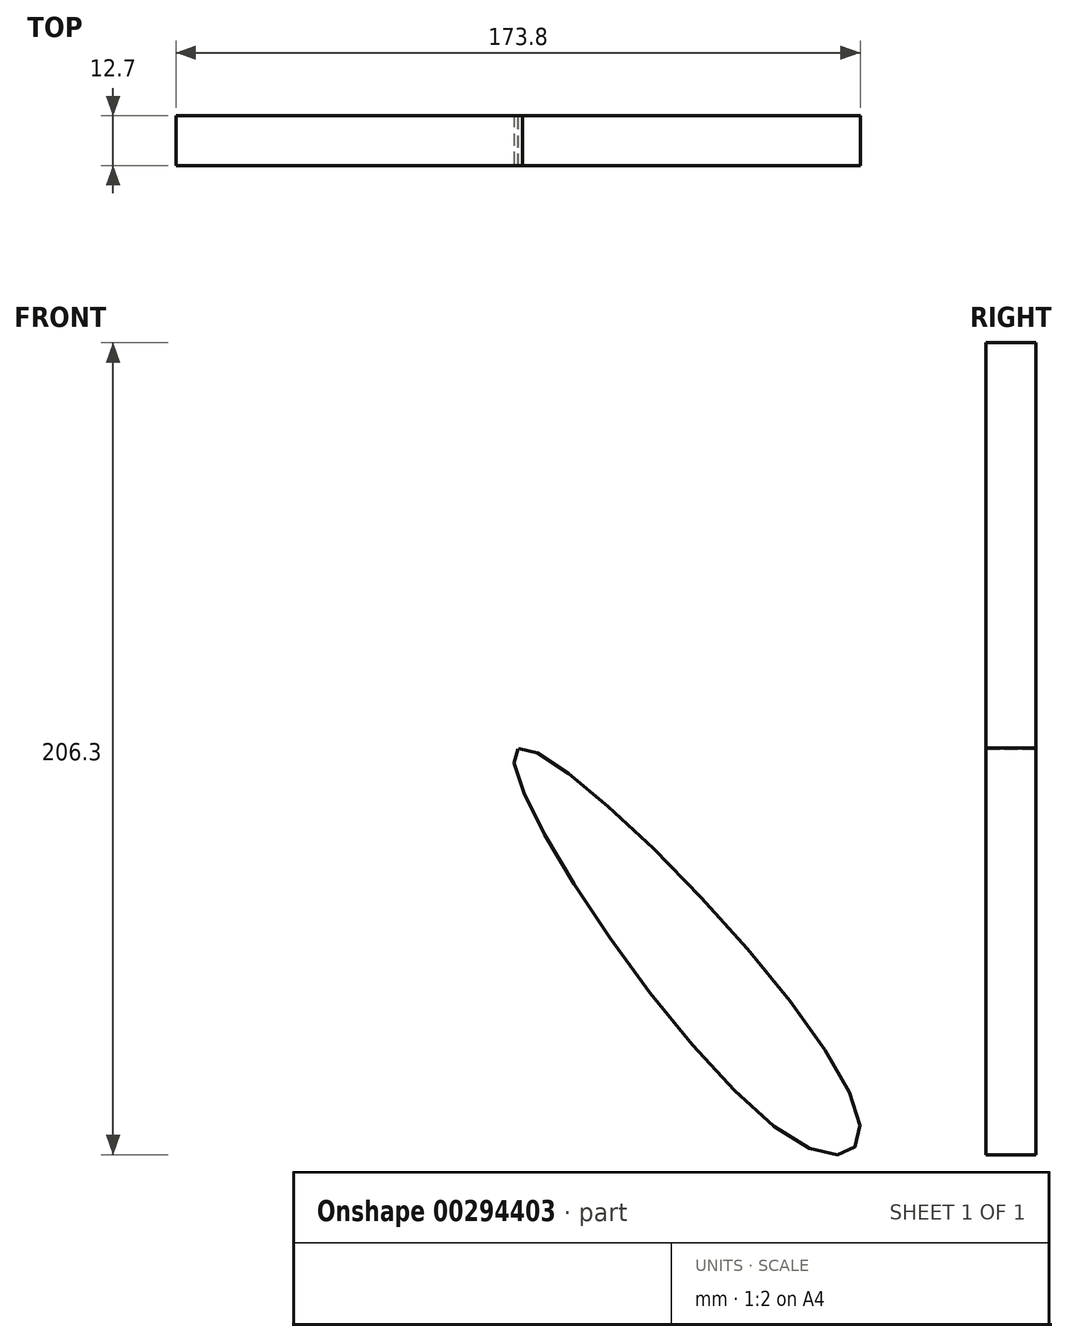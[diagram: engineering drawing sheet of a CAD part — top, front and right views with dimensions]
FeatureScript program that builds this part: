
annotation { "Feature Type Name" : "Feature", "Feature Type Description" : "" }
export const myFeature = defineFeature(function(context is Context, id is Id, definition is map)
    precondition{}
    {
        {
            var Q0;
            Q0=qCreatedBy(makeId("Front.planeOp"),FACE);
            var sketch = newSketch(context, id + "F0", { "sketchPlane" : qUnion([Q0])});
            skPoint(sketch, "E0", {"position": v(0.06, 0.02) * mm});
            skFitSpline(sketch, "E1", {"points": [v(0.06, 0.02) * mm, v(-86.65, 94.28) * mm, v(-70.95, 99.93) * mm, v(0.06, 0.02) * mm]});
            skFitSpline(sketch, "E2", {"points": [v(-0.1, -0.04) * mm, v(86.61, -94.3) * mm, v(70.9, -99.95) * mm, v(-0.1, -0.04) * mm]});
            skSolve(sketch);
        }
        {
            var Q0;
            Q0 = qSketchRegion(id + "F0", true);
            extrude(context, id + "F1", {"entities" : qUnion([Q0]), "depth" : 12.7 * mm, "offsetDistance" : 25.4 * mm});
        }
    });
